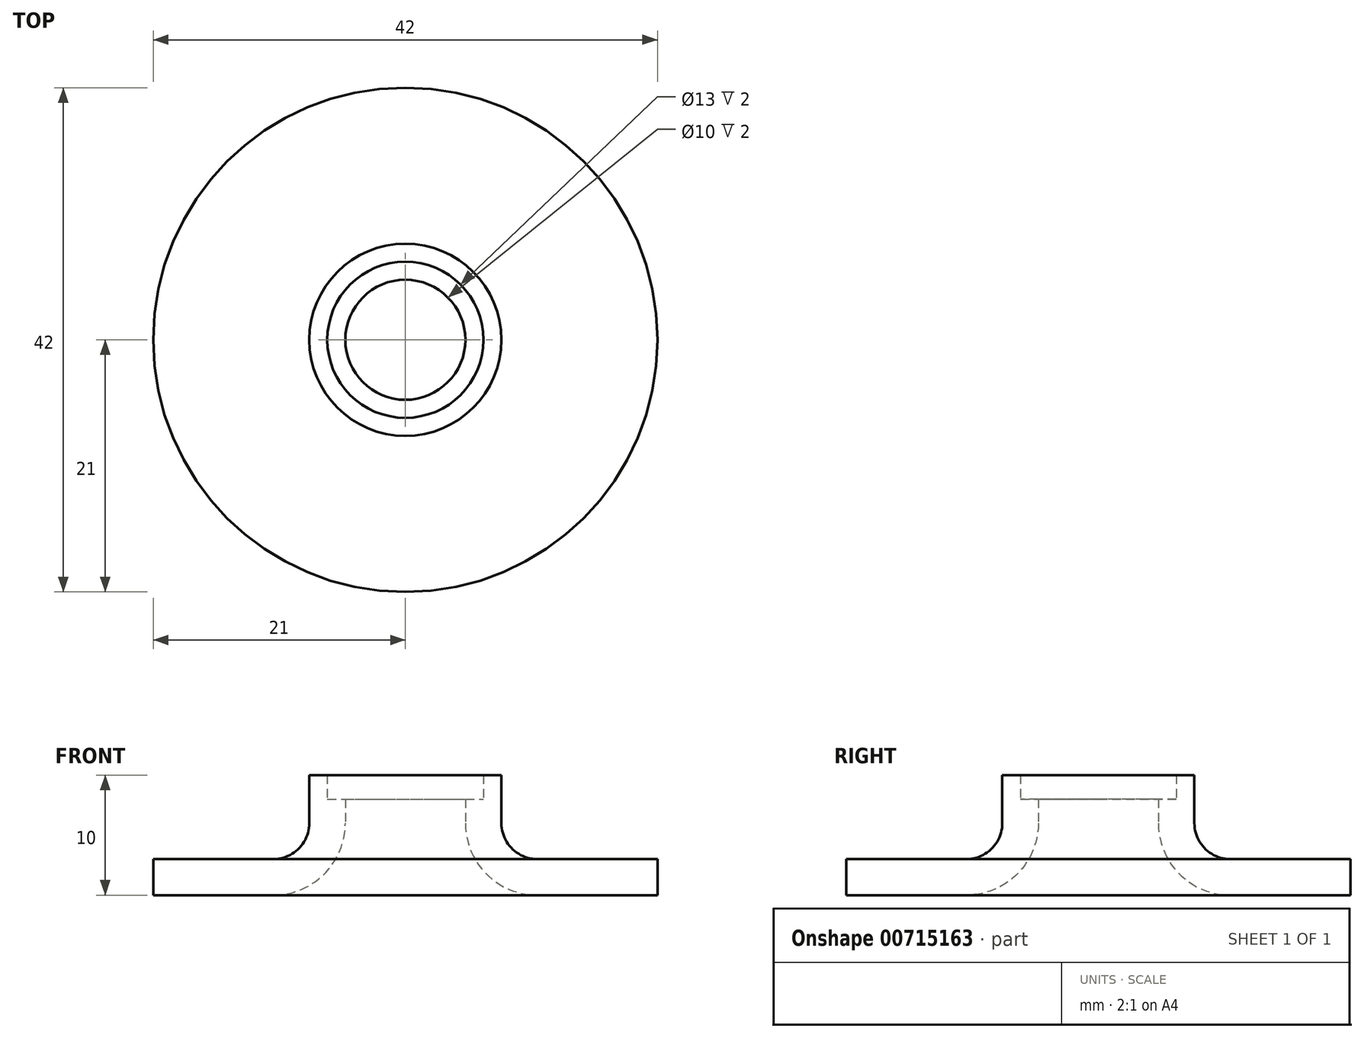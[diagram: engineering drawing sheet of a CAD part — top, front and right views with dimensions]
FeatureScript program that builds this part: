
annotation { "Feature Type Name" : "Feature", "Feature Type Description" : "" }
export const myFeature = defineFeature(function(context is Context, id is Id, definition is map)
    precondition{}
    {
        {
            var Q0;
            Q0=qCreatedBy(makeId("Front.planeOp"),FACE);
            var sketch = newSketch(context, id + "F0", { "sketchPlane" : qUnion([Q0])});
            skLineSegment(sketch, "E0", {"start": v(5, 8) * mm, "end": v(8, 8) * mm});
            skLineSegment(sketch, "E1", {"start": v(8, 8) * mm, "end": v(8, 6) * mm});
            skLineSegment(sketch, "E2", {"start": v(5, 8) * mm, "end": v(5, 6) * mm});
            skArc(sketch, "E3", {"start": v(8, 6) * mm, "mid": v(8.88, 3.88) * mm, "end": v(11, 3) * mm});
            skArc(sketch, "E4", {"start": v(5, 6) * mm, "mid": v(6.76, 1.76) * mm, "end": v(11, 0) * mm});
            skLineSegment(sketch, "E5", {"start": v(11, 3) * mm, "end": v(21, 3) * mm});
            skLineSegment(sketch, "E6", {"start": v(21, 3) * mm, "end": v(21, 0) * mm});
            skLineSegment(sketch, "E7", {"start": v(21, 0) * mm, "end": v(11, 0) * mm});
            skLineSegment(sketch, "E8", {"start": v(6.5, 8) * mm, "end": v(6.5, 10) * mm});
            skLineSegment(sketch, "E9", {"start": v(6.5, 10) * mm, "end": v(8, 10) * mm});
            skLineSegment(sketch, "E10", {"start": v(8, 10) * mm, "end": v(8, 8) * mm});
            skSolve(sketch);
        }
        {
            var Q0;
            Q0=qCreatedBy(makeId("Top.planeOp"),FACE);
            var sketch = newSketch(context, id + "F1", { "sketchPlane" : qUnion([Q0])});
            skCircle(sketch, "E11", {"center": v(0, 0) * mm, "radius": 13.09 * mm});
            skSolve(sketch);
        }
        {
            var Q0;
            Q0=makeQuery(id+"F0.imprint","IMPRINT",FACE,{"disambiguationData":[TD([[makeQuery(id+"F0.imprint","IMPRINT",EDGE,{"derivedFrom":sQuery(id+"F0.wireOp",EDGE,"E0")}),-1.0]])]});
            var Q1;
            {var subQ2=sQuery(id+"F0.wireOp",EDGE,"vws9b4sW-yg5V-vRfl-HaYm-ekbCcYCIv3qM");Q1=makeQuery(id+"F0.imprint","IMPRINT",FACE,{"disambiguationData":[TD([[makeQuery(id+"F0.imprint","IMPRINT",EDGE,{"derivedFrom":subQ2}),1.0]])]});}
            var Q2;
            {var subQ2=sQuery(id+"F0.wireOp",EDGE,"E8");Q2=makeQuery(id+"F0.imprint","IMPRINT",FACE,{"disambiguationData":[TD([[makeQuery(id+"F0.imprint","IMPRINT",EDGE,{"derivedFrom":subQ2}),-1.0]])]});}
            var Q3;
            Q3=sQuery(id+"F1.wireOp",EDGE,"E11");
            revolve(context, id + "F2", {"surfaceOperationType" : NewSurfaceOperationType.NEW, "entities" : qUnion([Q0, Q1, Q2]), "axis" : qUnion([Q3]), "revolveType" : RevolveType.FULL});
        }
    });
